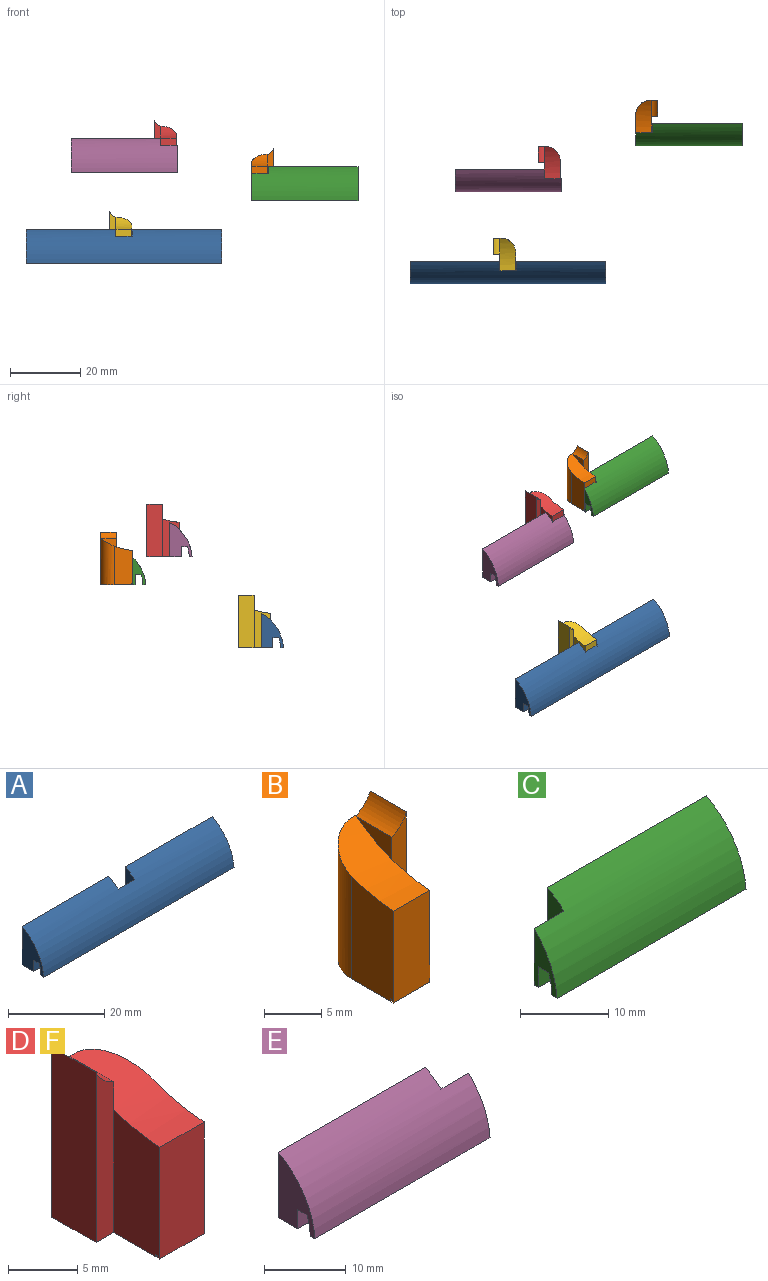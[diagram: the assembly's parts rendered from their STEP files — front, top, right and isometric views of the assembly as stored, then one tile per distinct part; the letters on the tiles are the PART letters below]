
ASSEMBLY  parts=6 mates=3
PART A: 13 faces, bbox 55.8x6.4x9.8 mm
  f0: plane 25.5x9.8mm, normal (0,1,0), area 249.9mm2, adj f1,f2,f8,f10
  f1: plane 55.8x3.38mm, normal (0,0,-1), area 175.9mm2, adj f0,f3,f4,f8,f9,f10,f11,f12
  f2: cylinder r=11.97mm len=55.8mm, axis (1,0,0), area 666.1mm2, adj f0,f3,f7,f8,f9,f10,f11,f12
  f3: plane 25.5x9.8mm, normal (0,1,0), area 249.9mm2, adj f1,f2,f9,f12
  f4: plane 55.8x2.89mm, normal (0,-1,0), area 161.4mm2, adj f1,f5,f8,f9
  f5: plane 55.8x1.69mm, normal (0,0,-1), area 94.1mm2, adj f4,f6,f8,f9
  f6: cylinder r=10.26mm len=55.8mm, axis (1,0,0), area 164.5mm2, adj f5,f7,f8,f9
  f7: plane 55.8x0.8mm, normal (0,0,-1), area 44.6mm2, adj f2,f6,f8,f9
  f8: plane 9.8x6.39mm, normal (-1,0,0), area 37.5mm2, adj f0,f1,f2,f4,f5,f6,f7
  f9: plane 9.8x6.39mm, normal (1,0,0), area 37.5mm2, adj f1,f2,f3,f4,f5,f6,f7
  f10: plane 9.8x2.7mm, normal (1,0,0), area 24.1mm2, adj f0,f1,f2,f11
  f11: plane 7.87x4.8mm, normal (0,1,0), area 37.8mm2, adj f1,f2,f10,f12
  f12: plane 9.8x2.7mm, normal (-1,0,0), area 24.1mm2, adj f1,f2,f3,f11
PART B: 16 faces, bbox 6.3x9.2x15 mm
  f0: plane 4.5x0.2mm, normal (0,0,-1), area 0.9mm2, adj f1,f2,f4,f13
  f1: plane 11.01x5.2mm, normal (-1,0,0), area 53.4mm2, adj f0,f4,f8,f11,f12,f13,f14,f15
  f2: plane 10.82x4.7mm, normal (1,0,0), area 48mm2, adj f0,f4,f5,f8,f11,f13,f14,f15
  f3: plane 0.11x0.08mm, normal (1,0,0), area 0mm2, adj f7,f9,f11
  f4: plane 9.84x4.5mm, normal (0,-1,0), area 44.3mm2, adj f0,f1,f2,f11
  f5: plane 15x1.8mm, normal (0,-1,0), area 24.9mm2, adj f2,f6,f8,f9,f10
  f6: plane 15x4.5mm, normal (1,0,0), area 67.5mm2, adj f5,f7,f8,f9
  f7: plane 15x2.3mm, normal (0,1,0), area 31.6mm2, adj f3,f6,f8,f9,f11,f12
  f8: plane 8.85x6.3mm, normal (0,0,-1), area 44.5mm2, adj f1,f2,f5,f6,f7,f12,f14
  f9: cylinder r=3.28mm len=4.5mm, axis (0,-1,0), area 11.8mm2, adj f3,f5,f6,f7,f10
  f10: plane 4.39x2.38mm, normal (-1,0,0), area 5.9mm2, adj f5,f9,f11
  f11: cylinder r=16.82mm len=9.2mm, axis (1,0,0), area 40.7mm2, adj f1,f2,f3,f4,f7,f10,f12
  f12: cylinder r=4mm len=13.28mm, axis (0,0,1), area 77.6mm2, adj f1,f7,f8,f11
  f13: plane 4.5x0.3mm, normal (0,1,0), area 1.3mm2, adj f0,f1,f2,f15
  f14: plane 4.5x0.3mm, normal (0,-1,0), area 1.3mm2, adj f1,f2,f8,f15
  f15: plane 4.5x0.15mm, normal (0,0,-1), area 0.7mm2, adj f1,f2,f13,f14
PART C: 11 faces, bbox 30.3x6.4x9.8 mm
  f0: plane 30.3x3.38mm, normal (0,0,-1), area 89.6mm2, adj f2,f3,f7,f8,f9,f10
  f1: cylinder r=11.97mm len=30.3mm, axis (1,0,0), area 354.4mm2, adj f2,f6,f7,f8,f9,f10
  f2: plane 25.5x9.8mm, normal (0,1,0), area 249.9mm2, adj f0,f1,f7,f9
  f3: plane 30.3x2.89mm, normal (0,-1,0), area 87.6mm2, adj f0,f4,f7,f10
  f4: plane 30.3x1.69mm, normal (0,0,-1), area 51.1mm2, adj f3,f5,f7,f10
  f5: cylinder r=10.26mm len=30.3mm, axis (1,0,0), area 89.4mm2, adj f4,f6,f7,f10
  f6: plane 30.3x0.8mm, normal (0,0,-1), area 24.2mm2, adj f1,f5,f7,f10
  f7: plane 9.8x6.39mm, normal (1,0,0), area 37.5mm2, adj f0,f1,f2,f3,f4,f5,f6
  f8: plane 7.87x4.8mm, normal (0,1,0), area 37.8mm2, adj f0,f1,f9,f10
  f9: plane 9.8x2.7mm, normal (-1,0,0), area 24.1mm2, adj f0,f1,f2,f8
  f10: plane 7.87x3.69mm, normal (-1,0,0), area 13.4mm2, adj f0,f1,f3,f4,f5,f6,f8
PART D: 15 faces, bbox 6.3x9.2x15 mm
  f0: plane 4.5x0.2mm, normal (0,0,-1), area 0.9mm2, adj f1,f2,f4,f12
  f1: plane 11.01x5.2mm, normal (1,0,0), area 53.4mm2, adj f0,f2,f7,f8,f10,f12,f13,f14
  f2: plane 9.84x4.5mm, normal (0,-1,0), area 44.3mm2, adj f0,f1,f4,f10
  f3: plane 15x2.3mm, normal (0,1,0), area 31.7mm2, adj f5,f7,f8,f9,f10
  f4: plane 10.82x4.7mm, normal (-1,0,0), area 48mm2, adj f0,f2,f6,f7,f10,f12,f13,f14
  f5: plane 15x4.5mm, normal (-1,0,0), area 67.5mm2, adj f3,f6,f7,f9
  f6: plane 15x1.8mm, normal (0,-1,0), area 25mm2, adj f4,f5,f7,f9,f11
  f7: plane 8.79x6.3mm, normal (0,0,-1), area 44.2mm2, adj f1,f3,f4,f5,f6,f8,f13
  f8: cylinder r=4mm len=13.28mm, axis (0,0,1), area 77.6mm2, adj f1,f3,f7,f10
  f9: cylinder r=3.28mm len=4.5mm, axis (0,-1,0), area 11.5mm2, adj f3,f5,f6,f11
  f10: cylinder r=16.82mm len=9.2mm, axis (-1,0,0), area 40.7mm2, adj f1,f2,f3,f4,f8,f11
  f11: plane 4.5x2.46mm, normal (1,0,0), area 6.2mm2, adj f6,f9,f10
  f12: plane 4.5x0.2mm, normal (0,1,0), area 0.9mm2, adj f0,f1,f4,f14
  f13: plane 4.5x0.2mm, normal (0,-1,0), area 0.9mm2, adj f1,f4,f7,f14
  f14: plane 4.5x0.21mm, normal (0,0,-1), area 0.9mm2, adj f1,f4,f12,f13
PART E: 11 faces, bbox 30.3x6.4x9.8 mm
  f0: plane 25.5x9.8mm, normal (0,1,0), area 249.9mm2, adj f1,f2,f7,f8
  f1: plane 30.3x3.38mm, normal (0,0,-1), area 89.6mm2, adj f0,f3,f7,f8,f9,f10
  f2: cylinder r=11.97mm len=30.3mm, axis (1,0,0), area 354.4mm2, adj f0,f6,f7,f8,f9,f10
  f3: plane 30.3x2.89mm, normal (0,-1,0), area 87.6mm2, adj f1,f4,f7,f10
  f4: plane 30.3x1.69mm, normal (0,0,-1), area 51.1mm2, adj f3,f5,f7,f10
  f5: cylinder r=10.26mm len=30.3mm, axis (1,0,0), area 89.4mm2, adj f4,f6,f7,f10
  f6: plane 30.3x0.8mm, normal (0,0,-1), area 24.2mm2, adj f2,f5,f7,f10
  f7: plane 9.8x6.39mm, normal (-1,0,0), area 37.5mm2, adj f0,f1,f2,f3,f4,f5,f6
  f8: plane 9.8x2.7mm, normal (1,0,0), area 24.1mm2, adj f0,f1,f2,f9
  f9: plane 7.87x4.8mm, normal (0,1,0), area 37.8mm2, adj f1,f2,f8,f10
  f10: plane 7.87x3.69mm, normal (1,0,0), area 13.4mm2, adj f1,f2,f3,f4,f5,f6,f9
PART F: same geometry as D
PLACE A t=(37.13,30.26,-3.71)mm
PLACE B t=(52.46,64.27,14.23)mm
PLACE C t=(76.03,109.36,14.23)mm
PLACE D t=(43.62,51.1,22.24)mm
PLACE E t=(49.99,56.34,42.94)mm
PLACE F t=(30.91,25.02,-3.71)mm
MATE fastened D.f2 <-> E.f9  axis (0,-1,0) through (39.12,46.4,22.24)mm
MATE fastened B.f4 <-> C.f8  axis (0,-1,0) through (65.16,59.62,14.23)mm
MATE fastened A.f11 <-> F.f2  axis (0,1,0) through (28.66,20.32,-3.71)mm
